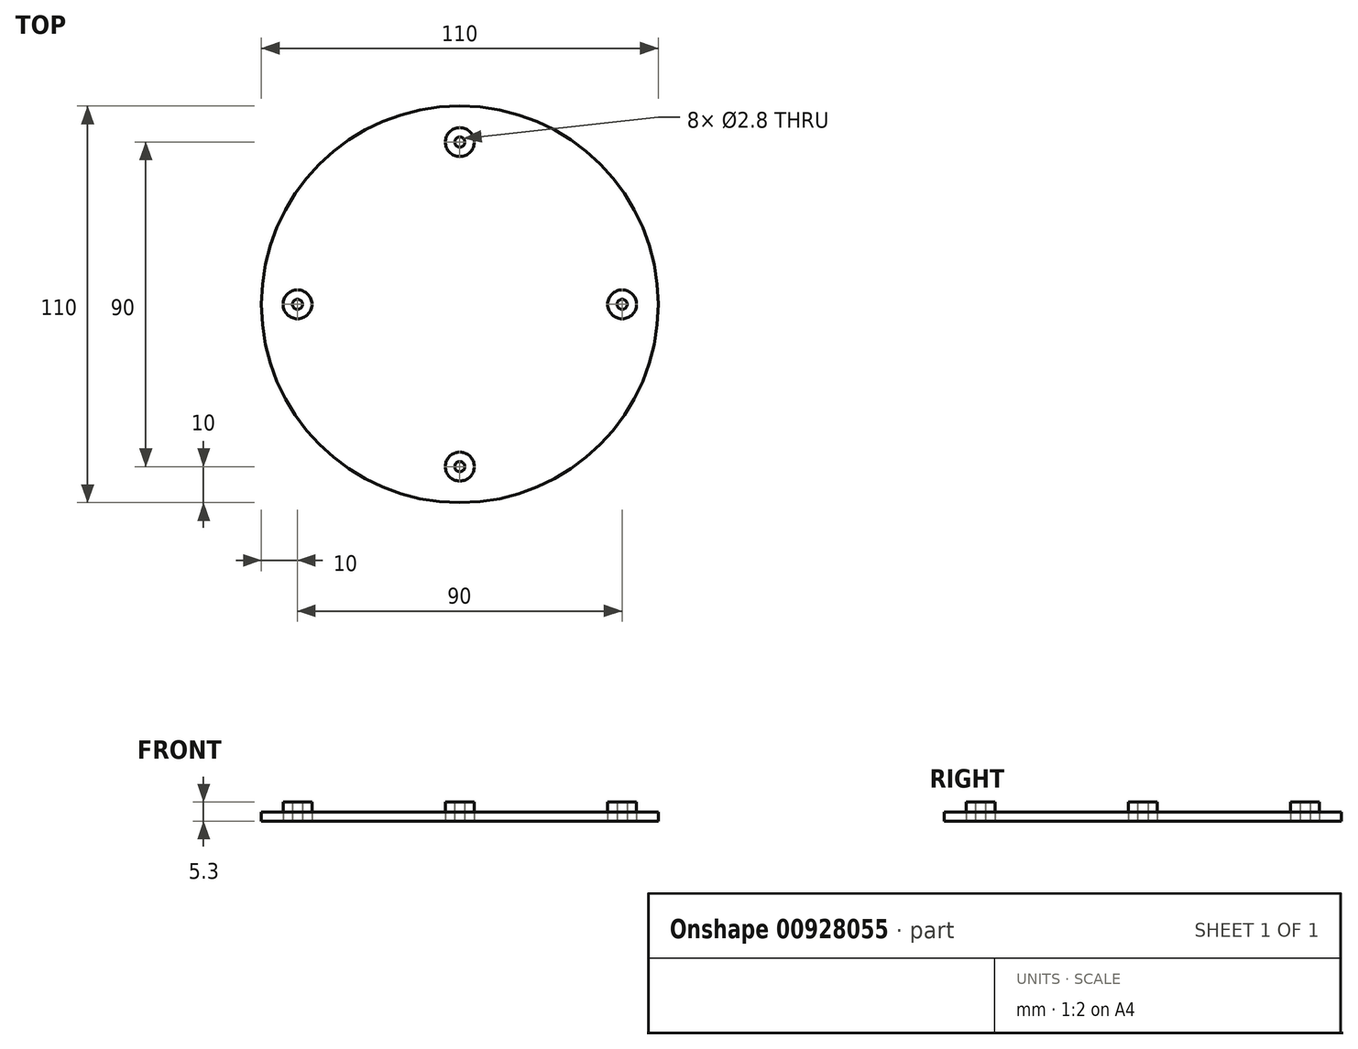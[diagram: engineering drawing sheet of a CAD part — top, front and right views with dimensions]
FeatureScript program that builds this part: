
annotation { "Feature Type Name" : "Feature", "Feature Type Description" : "" }
export const myFeature = defineFeature(function(context is Context, id is Id, definition is map)
    precondition{}
    {
        {
            var Q0;
            Q0=qCreatedBy(makeId("Top.planeOp"),FACE);
            var sketch = newSketch(context, id + "F0", { "sketchPlane" : qUnion([Q0])});
            skCircle(sketch, "E0", {"center": v(0, 0) * mm, "radius": 55 * mm});
            skSolve(sketch);
        }
        {
            var Q0;
            Q0=makeQuery(id+"F0.imprint","IMPRINT",FACE,{"disambiguationData":[TD([[makeQuery(id+"F0.imprint","IMPRINT",EDGE,{"derivedFrom":sQuery(id+"F0.wireOp",EDGE,"E0")}),1.0]])]});
            extrude(context, id + "F1", {"entities" : qUnion([Q0]), "depth" : 2.5 * mm, "offsetDistance" : 25 * mm});
        }
        {
            var Q0;
            Q0=makeQuery(id+"F1.opExtrude","CAP_FACE",FACE,{"disambiguationData":[OSD([sQuery(id+"F0.wireOp",EDGE,"E0")])],"isStart":true});
            var sketch = newSketch(context, id + "F2", { "sketchPlane" : qUnion([Q0])});
            skCircle(sketch, "E1", {"center": v(45, 0) * mm, "radius": 1.4 * mm});
            skCircle(sketch, "E2.1.0", {"center": v(0, 45) * mm, "radius": 1.4 * mm});
            skCircle(sketch, "E2.2.0", {"center": v(-45, 0) * mm, "radius": 1.4 * mm});
            skCircle(sketch, "E2.3.0", {"center": v(0, -45) * mm, "radius": 1.4 * mm});
            skPoint(sketch, "E2.center", {"position": v(0, 0) * mm});
            skCircle(sketch, "E3", {"center": v(45, 0) * mm, "radius": 4 * mm});
            skCircle(sketch, "E4.1.0", {"center": v(0, 45) * mm, "radius": 4 * mm});
            skCircle(sketch, "E4.2.0", {"center": v(-45, 0) * mm, "radius": 4 * mm});
            skCircle(sketch, "E4.3.0", {"center": v(0, -45) * mm, "radius": 4 * mm});
            skSolve(sketch);
        }
        {
            var Q0;
            Q0=makeQuery(id+"F2.imprint","IMPRINT",FACE,{"disambiguationData":[TD([[makeQuery(id+"F2.imprint","IMPRINT",EDGE,{"derivedFrom":sQuery(id+"F2.wireOp",EDGE,"E2.3.0")}),1.0]])]});
            var Q1;
            Q1=makeQuery(id+"F2.imprint","IMPRINT",FACE,{"disambiguationData":[TD([[makeQuery(id+"F2.imprint","IMPRINT",EDGE,{"derivedFrom":sQuery(id+"F2.wireOp",EDGE,"E2.2.0")}),1.0]])]});
            var Q2;
            Q2=makeQuery(id+"F2.imprint","IMPRINT",FACE,{"disambiguationData":[TD([[makeQuery(id+"F2.imprint","IMPRINT",EDGE,{"derivedFrom":sQuery(id+"F2.wireOp",EDGE,"E2.1.0")}),1.0]])]});
            var Q3;
            Q3=makeQuery(id+"F2.imprint","IMPRINT",FACE,{"disambiguationData":[TD([[makeQuery(id+"F2.imprint","IMPRINT",EDGE,{"derivedFrom":sQuery(id+"F2.wireOp",EDGE,"E1")}),1.0]])]});
            extrude(context, id + "F3", {"entities" : qUnion([Q0, Q1, Q2, Q3]), "operationType" : NewBodyOperationType.REMOVE, "endBound" : BoundingType.SYMMETRIC, "oppositeDirection" : true, "depth" : 25 * mm, "offsetDistance" : 25 * mm});
        }
        {
            var Q0;
            Q0=makeQuery(id+"F2.imprint","IMPRINT",FACE,{"disambiguationData":[TD([[makeQuery(id+"F2.imprint","IMPRINT",EDGE,{"derivedFrom":sQuery(id+"F2.wireOp",EDGE,"E2.2.0")}),-1.0]])]});
            var Q1;
            Q1=makeQuery(id+"F2.imprint","IMPRINT",FACE,{"disambiguationData":[TD([[makeQuery(id+"F2.imprint","IMPRINT",EDGE,{"derivedFrom":sQuery(id+"F2.wireOp",EDGE,"E2.3.0")}),-1.0]])]});
            var Q2;
            Q2=makeQuery(id+"F2.imprint","IMPRINT",FACE,{"disambiguationData":[TD([[makeQuery(id+"F2.imprint","IMPRINT",EDGE,{"derivedFrom":sQuery(id+"F2.wireOp",EDGE,"E1")}),-1.0]])]});
            var Q3;
            Q3=makeQuery(id+"F2.imprint","IMPRINT",FACE,{"disambiguationData":[TD([[makeQuery(id+"F2.imprint","IMPRINT",EDGE,{"derivedFrom":sQuery(id+"F2.wireOp",EDGE,"E2.1.0")}),-1.0]])]});
            var Q4;
            Q4=sQuery(id+"F2.wireOp",EDGE,"E4.3.0");
            var Q5;
            Q5=sQuery(id+"F2.wireOp",EDGE,"E3");
            var Q6;
            Q6=sQuery(id+"F2.wireOp",EDGE,"E4.1.0");
            var Q7;
            Q7=sQuery(id+"F2.wireOp",EDGE,"E4.2.0");
            extrude(context, id + "F4", {"entities" : qUnion([Q0, Q1, Q2, Q3]), "surfaceEntities" : qUnion([Q4, Q5, Q6, Q7]), "oppositeDirection" : true, "depth" : 5.3 * mm, "offsetDistance" : 25 * mm});
        }
    });
